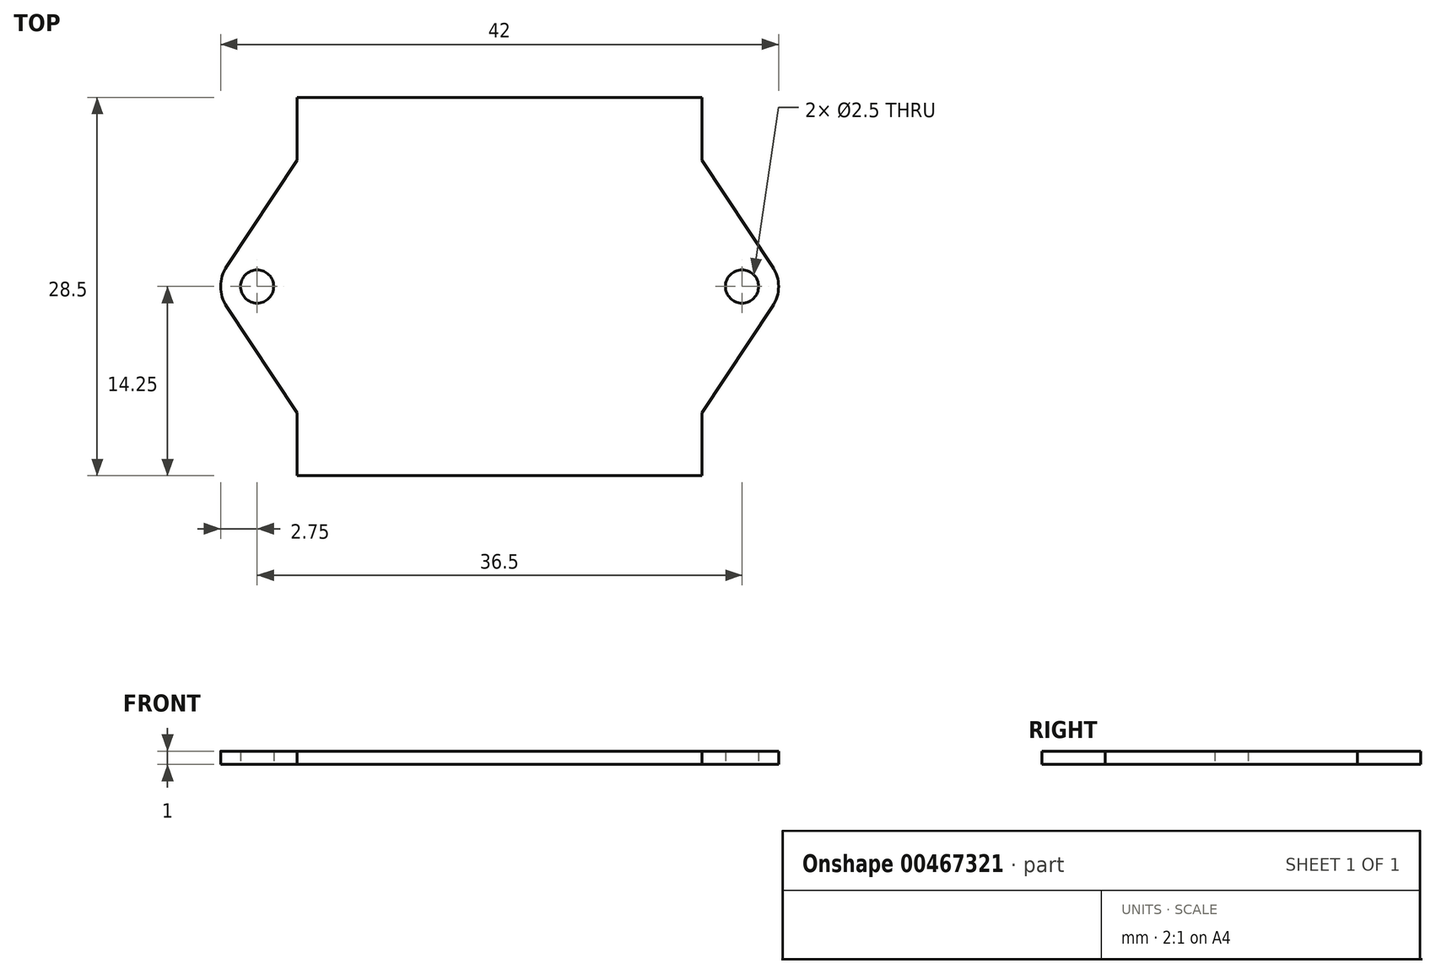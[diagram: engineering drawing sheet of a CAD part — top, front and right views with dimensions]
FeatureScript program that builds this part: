
annotation { "Feature Type Name" : "Feature", "Feature Type Description" : "" }
export const myFeature = defineFeature(function(context is Context, id is Id, definition is map)
    precondition{}
    {
        {
            var Q0;
            Q0=qCreatedBy(makeId("Top.planeOp"),FACE);
            var sketch = newSketch(context, id + "F0", { "sketchPlane" : qUnion([Q0])});
            skLineSegment(sketch, "E0.bottom", {"start": v(15.25, 14.25) * mm, "end": v(-15.25, 14.25) * mm});
            skLineSegment(sketch, "E0.top", {"start": v(15.25, -14.25) * mm, "end": v(-15.25, -14.25) * mm});
            skLineSegment(sketch, "E0.left", {"start": v(15.25, 14.25) * mm, "end": v(15.25, -14.25) * mm});
            skLineSegment(sketch, "E0.right", {"start": v(-15.25, 14.25) * mm, "end": v(-15.25, -14.25) * mm});
            skPoint(sketch, "E0.middle", {"position": v(0, 0) * mm});
            skCircle(sketch, "E1", {"center": v(-18.25, 0) * mm, "radius": 1.25 * mm});
            skCircle(sketch, "E2", {"center": v(18.25, 0) * mm, "radius": 1.25 * mm});
            skArc(sketch, "E3", {"start": v(-20.54, 1.52) * mm, "mid": v(-21, 0) * mm, "end": v(-20.54, -1.52) * mm});
            skArc(sketch, "E4", {"start": v(20.54, -1.52) * mm, "mid": v(21, 0) * mm, "end": v(20.54, 1.52) * mm});
            skLineSegment(sketch, "E5", {"start": v(-15.25, 9.5) * mm, "end": v(-20.54, 1.52) * mm});
            skLineSegment(sketch, "E6", {"start": v(-15.25, -9.5) * mm, "end": v(-20.54, -1.52) * mm});
            skLineSegment(sketch, "E7.MirrorCS", {"start": v(15.25, 9.5) * mm, "end": v(20.54, 1.52) * mm});
            skLineSegment(sketch, "E8.MirrorCS", {"start": v(15.25, -9.5) * mm, "end": v(20.54, -1.52) * mm});
            skPoint(sketch, "E9.orphan", {"position": v(-21.55, 0) * mm});
            skPoint(sketch, "E10.orphan", {"position": v(-20.99, -0.85) * mm});
            skPoint(sketch, "E11.orphan", {"position": v(21.55, 0) * mm});
            skPoint(sketch, "E12.orphan", {"position": v(20.99, -0.85) * mm});
            skPoint(sketch, "E13.MirrorCS.end.orphan", {"position": v(15.25, 9.5) * mm});
            skPoint(sketch, "E13.MirrorCS.start.orphan", {"position": v(15.25, -9.5) * mm});
            skSolve(sketch);
        }
        {
            var Q0;
            {var subQ3=sQuery(id+"F0.wireOp",EDGE,"E0.bottom");Q0=makeQuery(id+"F0.imprint","IMPRINT",FACE,{"disambiguationData":[TD([[makeQuery(id+"F0.imprint","IMPRINT",EDGE,{"derivedFrom":subQ3}),1.0]])]});}
            var Q1;
            Q1=makeQuery(id+"F0.imprint","IMPRINT",FACE,{"disambiguationData":[TD([[makeQuery(id+"F0.imprint","IMPRINT",EDGE,{"derivedFrom":sQuery(id+"F0.wireOp",EDGE,"E1")}),-1.0]])]});
            var Q2;
            Q2=makeQuery(id+"F0.imprint","IMPRINT",FACE,{"disambiguationData":[TD([[makeQuery(id+"F0.imprint","IMPRINT",EDGE,{"derivedFrom":sQuery(id+"F0.wireOp",EDGE,"E2")}),-1.0]])]});
            extrude(context, id + "F1", {"entities" : qUnion([Q0, Q1, Q2]), "depth" : 1 * mm});
        }
    });
